# Revit family: ASH_ArmitageShanks_WCSeats_Contour21_S4066
name_source: partatom
category: Plumbing Fixtures
revit_build: Autodesk Revit MEP 2012 (Build: 20110309_2315(x64)
units: mm (PartAtom-declared; Revit-internal decimal feet)

## types (4) — shared parameters
AccessibilityPerformance = DDA Compliant
Accessories = www.idealspec.co.uk
AreaUnits = millimeters
Assembly Code = C1030200
AssetType = Fixed
Brand = Armitage Shanks
ConnectionType = Mechanical
Description = Contour 21 seat no cover, top fixing hinges and retaining buffers
DurationUnit = year
ElementType = WCSEAT: Hinged seat that fits on the top of a water closet (WC) pan
ExpectedLife = 15
Features = Seat no cover, top fixing hinges and retaining buffers
Help = www.idealspec.co.uk/contact-us.html
IfcExportAs = IfcSanitaryTerminalType
IfcExportType = WCSEAT
InstallationInstructions = www.idealspec.co.uk/resources.html
LinearUnits = millimeters
ManufacturerURL = www.idealspec.co.uk
Material = Plastic
ModelReference = Contour 21 seat no cover, top fixing hinges and retaining buffers
NBSDescription = WC seats and covers
NBSReference = 45-35-70/391
NominalDepth = 409 mm
NominalHeight = 23 mm
NominalLength = 409 mm
SeatColor = White
SeatHasCover = No
SeatMaterial = Plastic
SeatType = RingSeat
Shape = Ring
Size = 410 x 380 x 23 mm
Space = Internal
SpareParts = www.fastpart-spares.co.uk
URL = www.idealspec.co.uk
Uniclass2 = Pr_40_20_93_95
Version = 2
VolumeUnits = Litres
WarrantyDescription = Manufacturers Warranty
WarrantyDurationParts = 5
WarrantyDurationUnit = year
zero-valued in all types: CWFU, Cost, Default Elevation, HWFU, WFU

## per-type parameters (varying)
| type | BIMObjectName | CodePerformance | Color | ECA | Finish | Model | ModelNumber | Name | NettWeight | NominalWidth | ProductInformation | SeatSKU | WRAS | WaterEfficientProduct |
| S406636 - Navy Seat | WCSEATS_ArmitageShanks_Contour21SeatOnly_S406636 |  | Navy | No | Blue 36 | S406636 | S406636 | WCSeats_Contour21-S4066_ArmitageShanks | 1.5 Kg | 84 mm | www.idealspec.co.uk/assets/datasheet/S406636 | ASH_ArmitageShanks _WCSeat _Blue36_render | No | No |
| S4066RN - Charcoal Seat | ASH_ArmitageShanks_WCSeats_Contour21SeatOnly_S4066 | DDA Compliant | Charcoal | Yes | Charcoal RN | S4066RN | S4066RN | WCSeats_Contour21SeatOnly-S4066_ArmitageShanks | 1.5Kg | 378 mm | www.idealspec.co.uk/resources.html | ASH_ArmitageShanks _WCSeat _CharcoalRN_render | Yes | Yes |
| S4066LJ - Light Grey Seat | ASH_ArmitageShanks_WCSeats_Contour21SeatOnly_S4066 | DDA Compliant | Light Grey | No | Grey LJ | S4066LJ | S4066LJ | WCSeats_Contour21SeatOnly-S4066_ArmitageShanks | 1.5Kg | 378 mm | www.idealspec.co.uk/resources.html | ASH_ArmitageShanks _WCSeat _LightGreyLJ_render | No | No |
| S406601 - White Seat | ASH_ArmitageShanks_WCSeats_Contour21SeatOnly_S406601 | DDA Compliant | White | No | White 01 | S406601 | S406601 | WCSeats_Contour21SeatOnly-S4066_ArmitageShanks | 1.5Kg | 378 mm | www.idealspec.co.uk/resources.html | ASH_ArmitageShanks _WCSeat _WhiteAC_render | No | No |

## geometry (parser evidence)
native form markers: Blend x2, Sweep x3
no freeform markers — native parametric forms only
